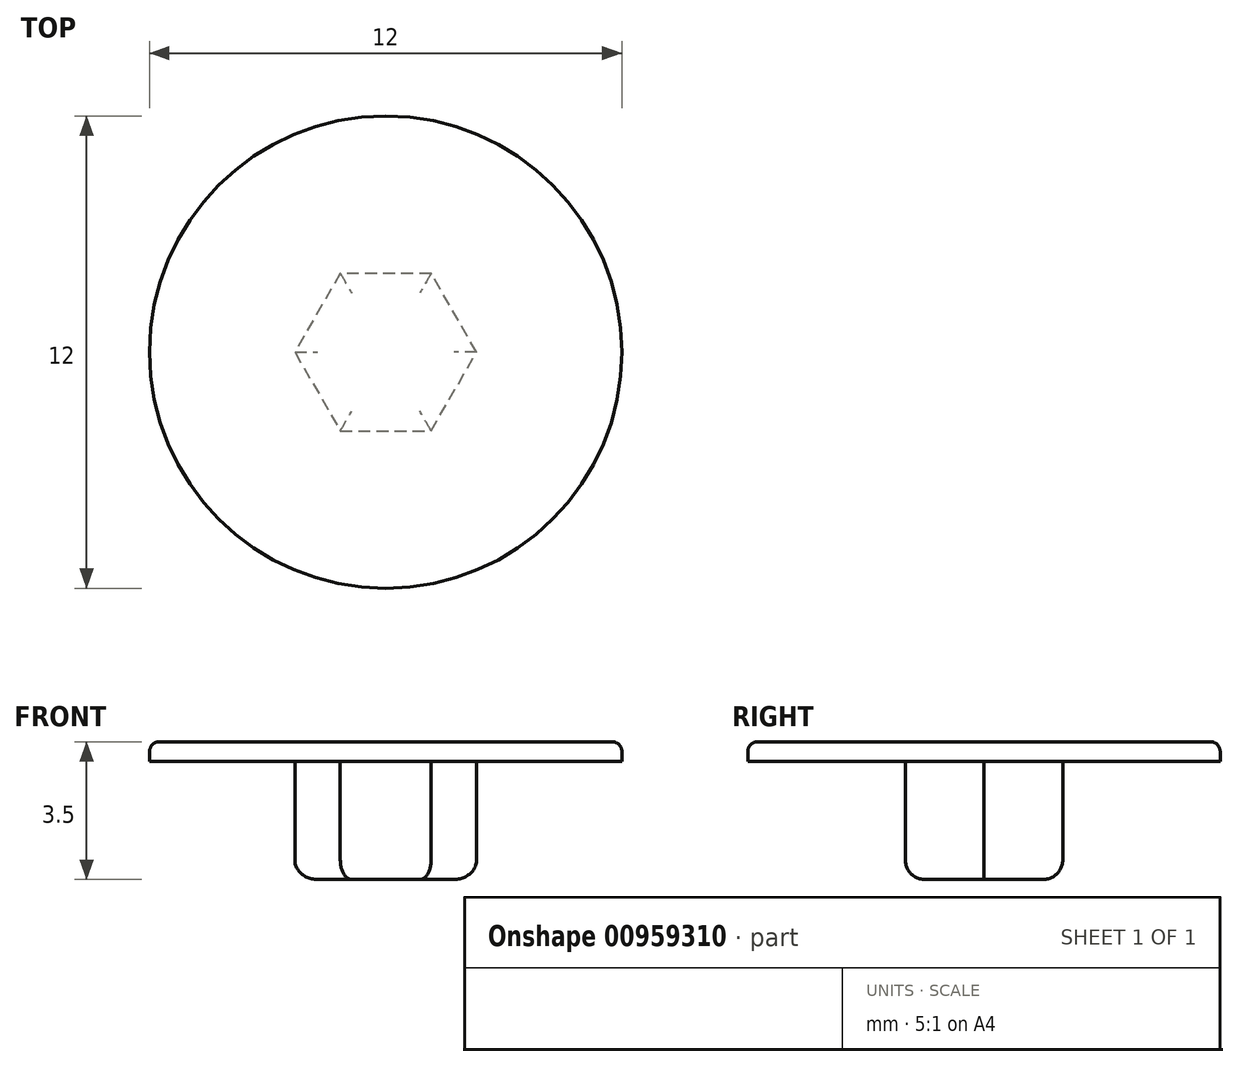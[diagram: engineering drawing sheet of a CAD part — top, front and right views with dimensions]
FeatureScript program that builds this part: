
annotation { "Feature Type Name" : "Feature", "Feature Type Description" : "" }
export const myFeature = defineFeature(function(context is Context, id is Id, definition is map)
    precondition{}
    {
        {
            var Q0;
            Q0=qCreatedBy(makeId("Top.planeOp"),FACE);
            var sketch = newSketch(context, id + "F0", { "sketchPlane" : qUnion([Q0])});
            skCircle(sketch, "E0", {"center": v(0, 0) * mm, "radius": 6 * mm});
            skSolve(sketch);
        }
        {
            var Q0;
            Q0 = qSketchRegion(id + "F0", true);
            extrude(context, id + "F1", {"entities" : qUnion([Q0]), "depth" : .5 * mm, "offsetDistance" : 25 * mm});
        }
        {
            var Q0;
            Q0=makeQuery(id+"F1.opExtrude","CAP_FACE",FACE,{"disambiguationData":[OSD([sQuery(id+"F0.wireOp",EDGE,"E0")])],"isStart":true});
            var sketch = newSketch(context, id + "F2", { "sketchPlane" : qUnion([Q0])});
            skCircle(sketch, "E1.cCircle", {"center": v(0, 0) * mm, "radius": 2 * mm, "construction": true});
            skLineSegment(sketch, "E1.0", {"start": v(1.15, -2) * mm, "end": v(-1.15, -2) * mm});
            skLineSegment(sketch, "E1.1", {"start": v(-1.15, -2) * mm, "end": v(-2.3, 0) * mm});
            skLineSegment(sketch, "E1.2", {"start": v(-2.3, 0) * mm, "end": v(-1.15, 2) * mm});
            skLineSegment(sketch, "E1.3", {"start": v(-1.15, 2) * mm, "end": v(1.15, 2) * mm});
            skLineSegment(sketch, "E1.4", {"start": v(1.15, 2) * mm, "end": v(2.3, 0) * mm});
            skLineSegment(sketch, "E1.5", {"start": v(2.3, 0) * mm, "end": v(1.15, -2) * mm});
            skPoint(sketch, "E1.0.midPoint", {"position": v(0, -2) * mm});
            skSolve(sketch);
        }
        {
            var Q0;
            Q0 = qSketchRegion(id + "F2", true);
            extrude(context, id + "F3", {"entities" : qUnion([Q0]), "operationType" : NewBodyOperationType.ADD, "depth" : 3 * mm, "offsetDistance" : 25 * mm});
        }
        {
            var Q0;
            Q0=makeQuery(id+"F3.opExtrude","CAP_FACE",FACE,{"disambiguationData":[OSD([sQuery(id+"F2.wireOp",EDGE,"E1.0"),sQuery(id+"F2.wireOp",EDGE,"E1.1"),sQuery(id+"F2.wireOp",EDGE,"E1.2"),sQuery(id+"F2.wireOp",EDGE,"E1.3"),sQuery(id+"F2.wireOp",EDGE,"E1.4"),sQuery(id+"F2.wireOp",EDGE,"E1.5")])],"isStart":false});
            fillet(context, id + "F4", {"entities" : qUnion([Q0]), "radius" : .5 * mm, "tangentPropagation" : true, "allowEdgeOverflow" : false});
        }
        {
            var Q0;
            Q0=makeQuery(id+"F1.opExtrude","CAP_EDGE",EDGE,{"disambiguationData":[OSD([sQuery(id+"F0.wireOp",EDGE,"E0")])],"isStart":false});
            fillet(context, id + "F5", {"entities" : qUnion([Q0]), "radius" : .25 * mm, "tangentPropagation" : true, "allowEdgeOverflow" : false});
        }
    });
